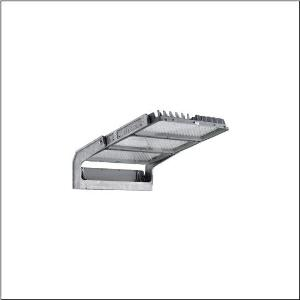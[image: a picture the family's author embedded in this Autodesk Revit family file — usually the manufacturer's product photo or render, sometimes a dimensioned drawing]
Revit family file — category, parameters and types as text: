
# Revit family: floodlight_fl_11_maxi_pro___rs12_5xa779228m01ab_5605
name_source: partatom
category: Lighting Fixtures
units: mm (PartAtom-declared; Revit-internal decimal feet)

## family parameters
Cut with Voids When Loaded = No
Host = Face
Light Source = No
Part Type = Normal
Room Calculation Point = No
Round Connector Dimension = Use Diameter
Shared = No

## types (1)
- --- (1 x LED, 179630 lm, 1571.1 W, 5700K)
    Apparent Load = 1571 VA
    CIE Flux Codes = 79 92 99 100 100
    Color Rendering = 80
    Color Temperature = 5700K
    Default Elevation = 1800 mm
    Description = Floodlight FL 11  maxi  pro floodlight; light control with lens of PMMA; cover panel of toughened safety glass, transparent; light distribution: RS12, rotationally symmetric direct distribution, LED; colour temperature: 5700K, rated luminous flux: 179.630lm, colour rendering: CRI > 80, light colour: 857; luminous efficacy: 114lm/W; brightness control: DMX+RDM; with terminal, 6-pole, max. 2.5mm², mains connection: 220..240V/380..400V AC, 50/60Hz, surge voltage resistance: line to ground: 10kV, LED service life up to 100,000h L90. Typical operating time: 1000h per year., ECG replaceable separately, LED unit replaceable without ESD environment, dustproof LED module, dimming range 10..100%; 1571W floodlight with 3x LED unit of diecast aluminium, coated grey; length: 1.003mm / width: 651mm / height: 338mm; mounting bracket, of diecast aluminium, uncoated, natural, equipment: Power, protection rating (complete): IP66; insulation class (complete): insulation class I (protective earthing); certification: CE, ENEC, VDE; ball protection: ball impact resistant, only for outdoor installations in the designated locations, permissible operating ambient temperature: -40..+55°C, permissible storage temperature: -40..+85°Cpackaging unit: 1 piece

Light Distribution: RS12
    Height = 320 mm
    Lamp = 1 x LED
    Lamp Light Flux = 179630 lm
    Lamp Power = 1571.1 W
    Lamp count = 1
    Length = 1002 mm
    Luminous efficacy = 114 lm/W
    Manufacturer = Siteco
    ModVariant = No
    Model = 5XA779228M01AB
    Mounting Place = Ceiling
    Mounting Type = Surface mounted
    Number of Poles = 1
    OnlyDefault = Yes
    Power Factor = 1
    Product Name = Floodlight FL 11 maxi pro | RS12
    Product group = floodlight | ceiling mounted
    ProductGroupID = 303
    Protection Class = Protection class I
    Protection Degree = IP 66
    RLX_Detail_Level = 1
    RLX_Emergency_Light_Flux = 0 lm
    RLX_Emergency_Type = 0
    RLX_Emergency_Type_DB = No
    RlxData = <blob elided: 40301 chars, md5=f3afa688>
    Socket = socket
    Standby Power = 0 W
    System Light Flux = 179630 lm
    System Power = 1571 W
    Type Comments = factory setting: luminous flux: 100 % | dim-lin: 255 | 1060 mA
    Type Image = l_1356210.jpg
    URL = http://relux.com
    VarID = @adj_033467
    Voltage = 0 V
    Weight = 0.00 kg
    Width = 655 mm

## geometry (parser evidence)
native form markers: Blend x4, Sweep x12
no freeform markers — native parametric forms only
